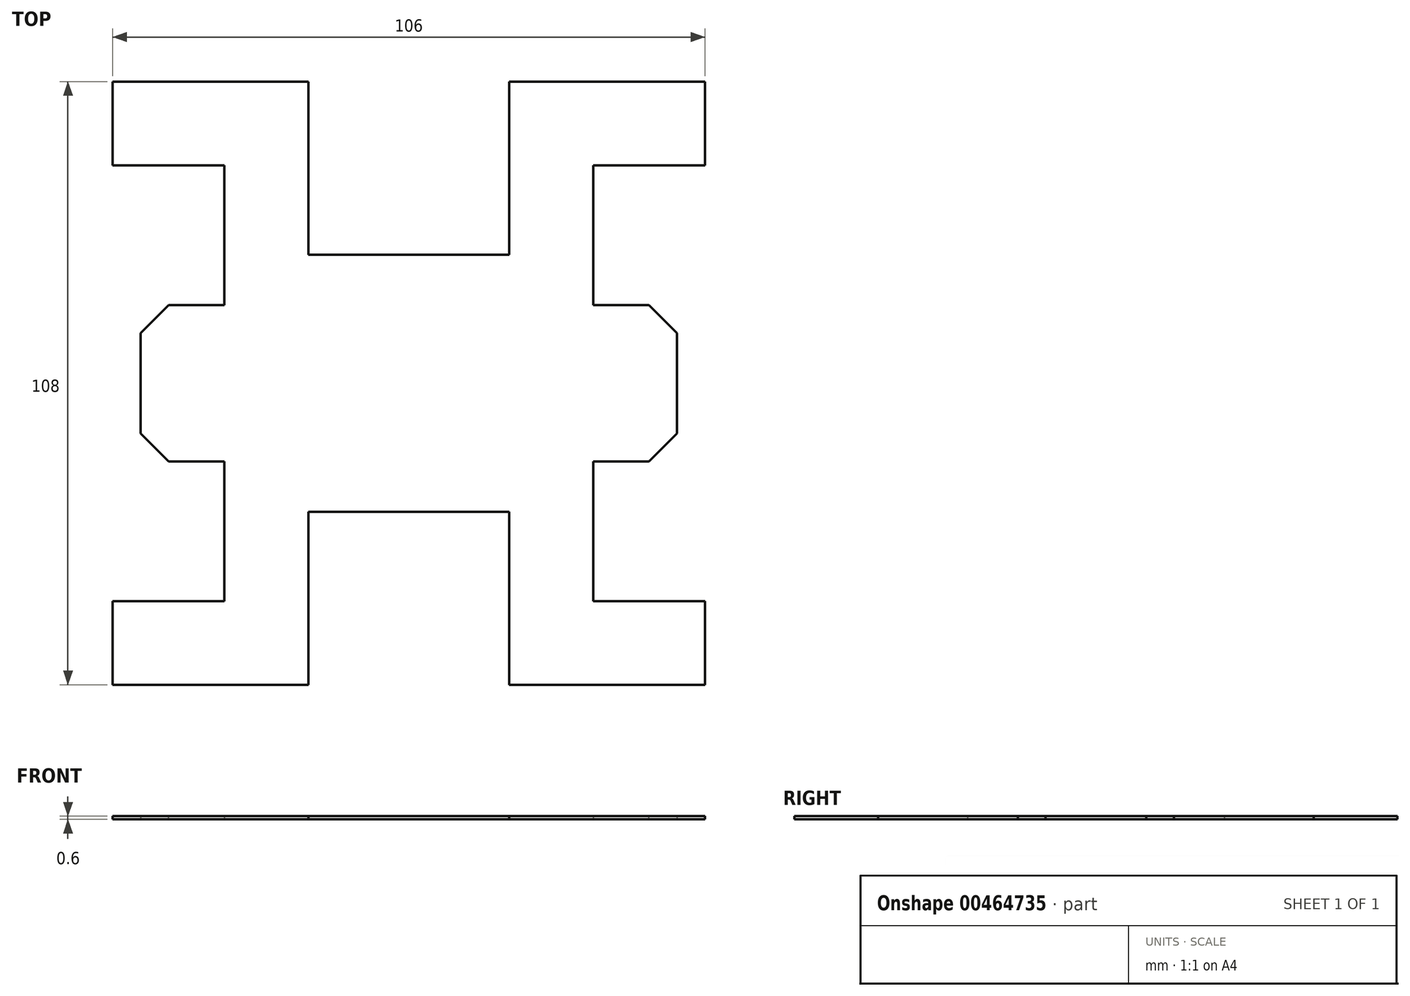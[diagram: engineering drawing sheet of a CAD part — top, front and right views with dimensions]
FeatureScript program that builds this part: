
annotation { "Feature Type Name" : "Feature", "Feature Type Description" : "" }
export const myFeature = defineFeature(function(context is Context, id is Id, definition is map)
    precondition{}
    {
        {
            var Q0;
            Q0=qCreatedBy(makeId("Top.planeOp"),FACE);
            var sketch = newSketch(context, id + "F0", { "sketchPlane" : qUnion([Q0])});
            skLineSegment(sketch, "E0", {"start": v(-48, 0) * mm, "end": v(-48, 14) * mm});
            skLineSegment(sketch, "E1", {"start": v(-48, 14) * mm, "end": v(-33, 14) * mm});
            skLineSegment(sketch, "E2", {"start": v(-33, 14) * mm, "end": v(-33, 39) * mm});
            skLineSegment(sketch, "E3", {"start": v(-33, 39) * mm, "end": v(-53, 39) * mm});
            skLineSegment(sketch, "E4", {"start": v(-53, 39) * mm, "end": v(-53, 54) * mm});
            skLineSegment(sketch, "E5", {"start": v(-53, 54) * mm, "end": v(-18, 54) * mm});
            skLineSegment(sketch, "E6", {"start": v(-18, 54) * mm, "end": v(-18, 23) * mm});
            skLineSegment(sketch, "E7.MirrorCS", {"start": v(-48, 0) * mm, "end": v(-48, -14) * mm});
            skLineSegment(sketch, "E8.MirrorCS", {"start": v(-48, -14) * mm, "end": v(-33, -14) * mm});
            skLineSegment(sketch, "E9.MirrorCS", {"start": v(-33, -14) * mm, "end": v(-33, -39) * mm});
            skLineSegment(sketch, "E10.MirrorCS", {"start": v(-33, -39) * mm, "end": v(-53, -39) * mm});
            skLineSegment(sketch, "E11.MirrorCS", {"start": v(-53, -39) * mm, "end": v(-53, -54) * mm});
            skLineSegment(sketch, "E12.MirrorCS", {"start": v(-18, -54) * mm, "end": v(-18, -23) * mm});
            skLineSegment(sketch, "E13.MirrorCS", {"start": v(-53, -54) * mm, "end": v(-18, -54) * mm});
            skLineSegment(sketch, "E14.MirrorCS", {"start": v(53, -54) * mm, "end": v(18, -54) * mm});
            skLineSegment(sketch, "E15.MirrorCS", {"start": v(53, -39) * mm, "end": v(53, -54) * mm});
            skLineSegment(sketch, "E16.MirrorCS", {"start": v(18, -54) * mm, "end": v(18, -23) * mm});
            skLineSegment(sketch, "E17.MirrorCS", {"start": v(48, 0) * mm, "end": v(48, 14) * mm});
            skLineSegment(sketch, "E18.MirrorCS", {"start": v(48, 14) * mm, "end": v(33, 14) * mm});
            skLineSegment(sketch, "E19.MirrorCS", {"start": v(33, 14) * mm, "end": v(33, 39) * mm});
            skLineSegment(sketch, "E20.MirrorCS", {"start": v(33, 39) * mm, "end": v(53, 39) * mm});
            skLineSegment(sketch, "E21.MirrorCS", {"start": v(18, 54) * mm, "end": v(18, 23) * mm});
            skLineSegment(sketch, "E22.MirrorCS", {"start": v(48, 0) * mm, "end": v(48, -14) * mm});
            skLineSegment(sketch, "E23.MirrorCS", {"start": v(53, 39) * mm, "end": v(53, 54) * mm});
            skLineSegment(sketch, "E24.MirrorCS", {"start": v(53, 54) * mm, "end": v(18, 54) * mm});
            skLineSegment(sketch, "E25.MirrorCS", {"start": v(48, -14) * mm, "end": v(33, -14) * mm});
            skLineSegment(sketch, "E26.MirrorCS", {"start": v(33, -39) * mm, "end": v(53, -39) * mm});
            skLineSegment(sketch, "E27.MirrorCS", {"start": v(33, -14) * mm, "end": v(33, -39) * mm});
            skLineSegment(sketch, "E28.0", {"start": v(-18, 23) * mm, "end": v(18, 23) * mm});
            skLineSegment(sketch, "E29.0", {"start": v(18, -23) * mm, "end": v(0, -23) * mm});
            skLineSegment(sketch, "E29.1", {"start": v(-18, -23) * mm, "end": v(0, -23) * mm});
            skSolve(sketch);
        }
        {
            var Q0;
            Q0 = qSketchRegion(id + "F0", true);
            extrude(context, id + "F1", {"entities" : qUnion([Q0]), "depth" : .6 * mm});
        }
        {
            var Q0;
            Q0=makeQuery(id+"F1.opExtrude","SWEPT_EDGE",EDGE,{"disambiguationData":[OSD([sQuery(id+"F0.wireOp",EDGE,"E0"),sQuery(id+"F0.wireOp",EDGE,"E1")])]});
            var Q1;
            Q1=makeQuery(id+"F1.opExtrude","SWEPT_EDGE",EDGE,{"disambiguationData":[OSD([sQuery(id+"F0.wireOp",EDGE,"E7.MirrorCS"),sQuery(id+"F0.wireOp",EDGE,"E8.MirrorCS")])]});
            var Q2;
            Q2=makeQuery(id+"F1.opExtrude","SWEPT_EDGE",EDGE,{"disambiguationData":[OSD([sQuery(id+"F0.wireOp",EDGE,"E17.MirrorCS"),sQuery(id+"F0.wireOp",EDGE,"E18.MirrorCS")])]});
            var Q3;
            Q3=makeQuery(id+"F1.opExtrude","SWEPT_EDGE",EDGE,{"disambiguationData":[OSD([sQuery(id+"F0.wireOp",EDGE,"E22.MirrorCS"),sQuery(id+"F0.wireOp",EDGE,"E25.MirrorCS")])]});
            chamfer(context, id + "F2", {"entities" : qUnion([Q0, Q1, Q2, Q3]), "width" : 5 * mm, "tangentPropagation" : true});
        }
    });
